# Revit family: Gleitplatte 2x M16
name_source: partatom
category: HLS-Bauteile
revit_build: Autodesk Revit 2017 (Build: 20190507_1515(x64)
units: mm (PartAtom-declared; Revit-internal decimal feet)

## family parameters
Arbeitsebenenbasiert = Ja
Beim Laden mit Abzugskörper schneiden = Nein
Bemaßung runder Anschluss = Durchmesser verwenden
Gemeinsam genutzt = Ja
Immer vertikal = Nein
OmniClass-Nummer = 23.75.00.00
OmniClass-Titel = Climate Control (HVAC)
Raumberechnungspunkt = Nein
Teiletyp = Normal

## types (3) — shared parameters
Abstand zur Außenkante = 25 mm  [stored 0.082021 ft]
Achsmaß = 25 mm
Anschluss = M16
Anschlüsse = 6kt-Mutter parametrik : Mutter M16 (4120522)
Anzahl Anschlüsse = 2
Breite = 100 mm  [stored 0.328084 ft]
Fabrikat = MEFA
Firma = MEFA Befestigungs- und Montagesysteme GmbH
Höhe Gewindeanschluss HGW = 15 mm  [stored 0.0492126 ft]
Kurztext2 = Anschluss 2 x M16
Mengeneinheit = St
Stärke = 8 mm  [stored 0.0262467 ft]
vpe = 1 St
zero-valued in all types: Vorgabe-Ansicht

## per-type parameters (varying)
| type | Artikelnummer | EAN | Gewicht | Gewicht pro Bauteil | Kurztext1 | Länge | max. zul. Last |
| Gleitplatte 200x100x 8, 2x M16 | 0771163 | 4250928418203 | 1.36 kg | 1.36 kg | Gleitplatte 200 x 100 x 8 | 200 mm  [stored 0.656168 ft] | 3.00 kN |
| Gleitplatte 150x100x 8, 2x M16 | 0771164 | 4250928418210 | 1.04 kg | 1.04 kg | Gleitplatte 150 x 100 x 8 | 150 mm | 4.80 kN |
| Gleitplatte 250x100x 8, 2x M16 | 0771465 | 4250928418302 | 1.67 kg | 1.67 kg | Gleitplatte 250 x 100 x 8 | 250 mm | 2.20 kN |

note: [stored X ft] marks values corroborated as IEEE doubles in the binary element streams (Revit-internal decimal feet)

## geometry (parser evidence)
native form markers: Sweep x3
no freeform markers — native parametric forms only
